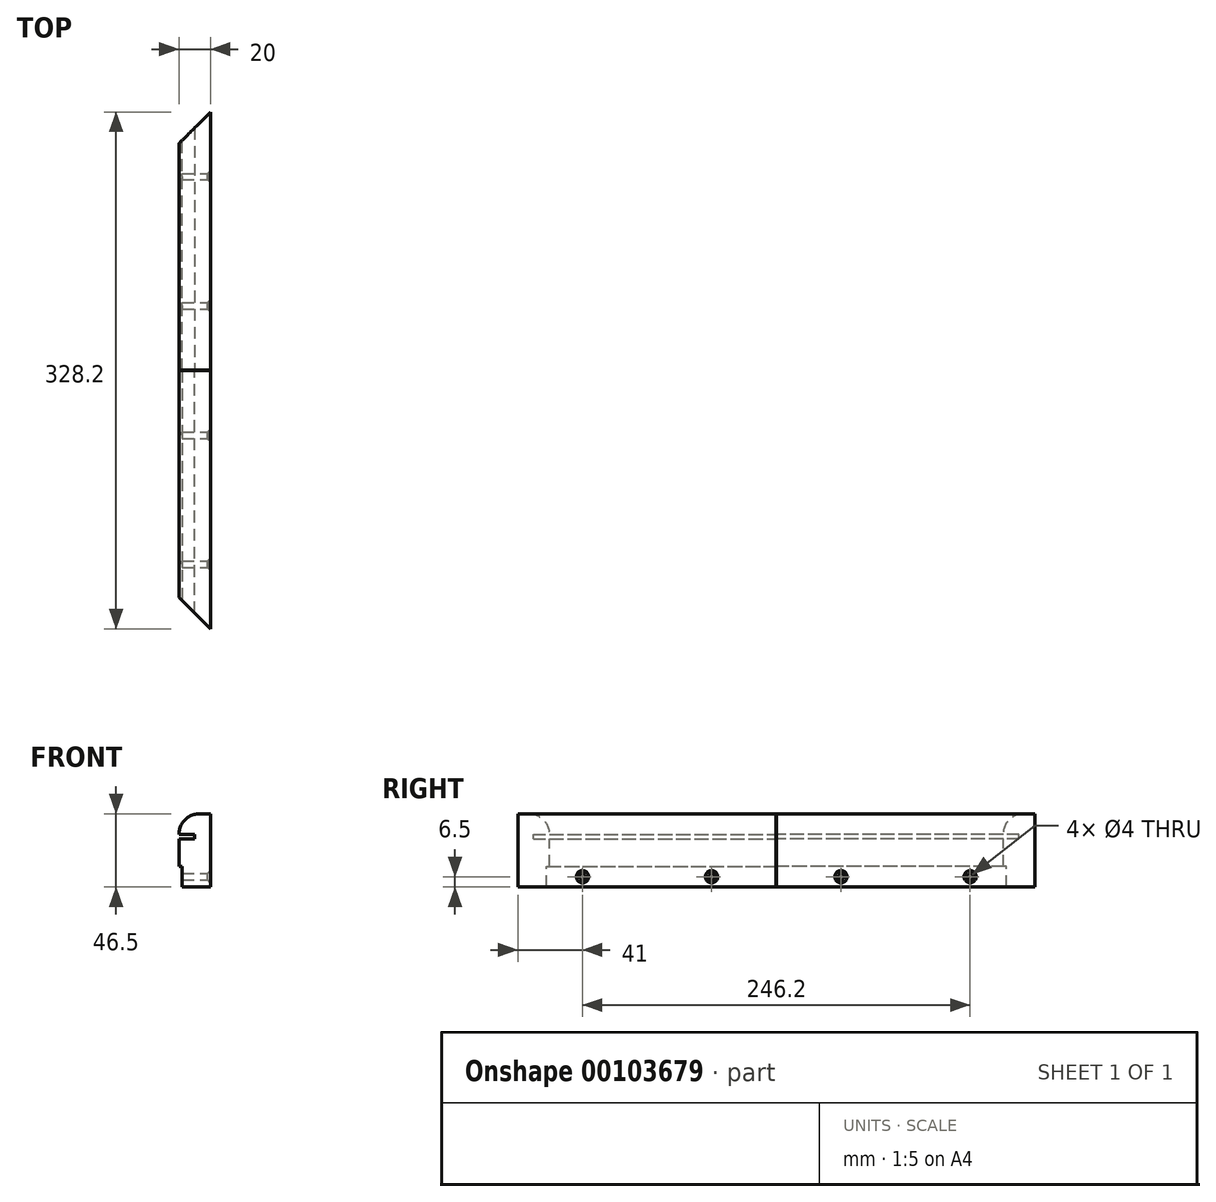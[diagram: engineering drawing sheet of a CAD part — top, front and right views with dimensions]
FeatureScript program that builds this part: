
annotation { "Feature Type Name" : "Feature", "Feature Type Description" : "" }
export const myFeature = defineFeature(function(context is Context, id is Id, definition is map)
    precondition{}
    {
        {
            var Q0;
            Q0=qCreatedBy(makeId("Front.planeOp"),FACE);
            var sketch = newSketch(context, id + "F0", { "sketchPlane" : qUnion([Q0])});
            skLineSegment(sketch, "E0.bottom", {"start": v(10, 23.25) * mm, "end": v(-10, 23.25) * mm});
            skLineSegment(sketch, "E0.top", {"start": v(10, -23.25) * mm, "end": v(-10, -23.25) * mm});
            skLineSegment(sketch, "E0.left", {"start": v(10, 23.25) * mm, "end": v(10, -23.25) * mm});
            skLineSegment(sketch, "E0.right", {"start": v(-10, 23.25) * mm, "end": v(-10, -23.25) * mm});
            skPoint(sketch, "E0.middle", {"position": v(0, 0) * mm});
            skSolve(sketch);
        }
        {
            var Q0;
            Q0=makeQuery(id+"F0.imprint","IMPRINT",FACE,{"disambiguationData":[TD([[makeQuery(id+"F0.imprint","IMPRINT",EDGE,{"derivedFrom":sQuery(id+"F0.wireOp",EDGE,"E0.bottom")}),1.0]])]});
            extrude(context, id + "F1", {"entities" : qUnion([Q0]), "depth" : 164 * mm});
        }
        {
            var Q0;
            Q0=makeQuery(id+"F1.opExtrude","SWEPT_FACE",FACE,{"disambiguationData":[OSD([sQuery(id+"F0.wireOp",EDGE,"E0.right")])]});
            var sketch = newSketch(context, id + "F2", { "sketchPlane" : qUnion([Q0])});
            skLineSegment(sketch, "E1.bottom", {"start": v(0, 10.25) * mm, "end": v(164, 10.25) * mm});
            skLineSegment(sketch, "E1.top", {"start": v(0, 7.15) * mm, "end": v(164, 7.15) * mm});
            skLineSegment(sketch, "E1.left", {"start": v(0, 10.25) * mm, "end": v(0, 7.15) * mm});
            skLineSegment(sketch, "E1.right", {"start": v(164, 10.25) * mm, "end": v(164, 7.15) * mm});
            skLineSegment(sketch, "E2.bottom", {"start": v(0, -23.25) * mm, "end": v(164, -23.25) * mm});
            skLineSegment(sketch, "E2.top", {"start": v(0, -10.25) * mm, "end": v(164, -10.25) * mm});
            skLineSegment(sketch, "E2.left", {"start": v(0, -23.25) * mm, "end": v(0, -10.25) * mm});
            skLineSegment(sketch, "E2.right", {"start": v(164, -23.25) * mm, "end": v(164, -10.25) * mm});
            skSolve(sketch);
        }
        {
            var Q0;
            Q0=makeQuery(id+"F2.imprint","IMPRINT",FACE,{"disambiguationData":[TD([[makeQuery(id+"F2.imprint","IMPRINT",EDGE,{"derivedFrom":sQuery(id+"F2.wireOp",EDGE,"E1.bottom")}),-1.0]])]});
            extrude(context, id + "F3", {"entities" : qUnion([Q0]), "operationType" : NewBodyOperationType.REMOVE, "oppositeDirection" : true, "depth" : 10 * mm});
        }
        {
            var Q0;
            {var subQ0=sQuery(id+"F0.wireOp",EDGE,"E0.right");var subQ2=sQuery(id+"F0.wireOp",EDGE,"E0.top");Q0=makeQuery(id+"F3.boolean.opBoolean","SPLIT",FACE,{"disambiguationData":[TD([makeQuery(id+"F1.opExtrude","SWEPT_FACE",FACE,{"disambiguationData":[OSD([subQ2])]})])],"derivedFrom":makeQuery(id+"F1.opExtrude","SWEPT_FACE",FACE,{"disambiguationData":[OSD([subQ0])]})});}
            var sketch = newSketch(context, id + "F4", { "sketchPlane" : qUnion([Q0])});
            skLineSegment(sketch, "E3.bottom", {"start": v(0, -23.25) * mm, "end": v(164, -23.25) * mm});
            skLineSegment(sketch, "E3.top", {"start": v(0, -10.25) * mm, "end": v(164, -10.25) * mm});
            skLineSegment(sketch, "E3.left", {"start": v(0, -23.25) * mm, "end": v(0, -10.25) * mm});
            skLineSegment(sketch, "E3.right", {"start": v(164, -23.25) * mm, "end": v(164, -10.25) * mm});
            skSolve(sketch);
        }
        {
            var Q0;
            Q0=makeQuery(id+"F4.imprint","IMPRINT",FACE,{"disambiguationData":[TD([[makeQuery(id+"F4.imprint","IMPRINT",EDGE,{"derivedFrom":sQuery(id+"F4.wireOp",EDGE,"E3.bottom")}),-1.0]])]});
            extrude(context, id + "F5", {"entities" : qUnion([Q0]), "operationType" : NewBodyOperationType.REMOVE, "oppositeDirection" : true, "depth" : 2 * mm});
        }
        {
            var Q0;
            Q0=makeQuery(id+"F1.opExtrude","SWEPT_FACE",FACE,{"disambiguationData":[OSD([sQuery(id+"F0.wireOp",EDGE,"E0.bottom")])]});
            var sketch = newSketch(context, id + "F6", { "sketchPlane" : qUnion([Q0])});
            skLineSegment(sketch, "E4.bottom", {"start": v(10, 0) * mm, "end": v(-10, 0) * mm, "construction": true});
            skLineSegment(sketch, "E4.top", {"start": v(10, -20) * mm, "end": v(-10, -20) * mm, "construction": true});
            skLineSegment(sketch, "E4.left", {"start": v(10, 0) * mm, "end": v(10, -20) * mm, "construction": true});
            skLineSegment(sketch, "E4.right", {"start": v(-10, 0) * mm, "end": v(-10, -20) * mm, "construction": true});
            skLineSegment(sketch, "E5", {"start": v(-10, -20) * mm, "end": v(10, 0) * mm});
            skLineSegment(sketch, "E6", {"start": v(-10, -20) * mm, "end": v(-10, 0) * mm});
            skLineSegment(sketch, "E7", {"start": v(-10, 0) * mm, "end": v(10, 0) * mm});
            skSolve(sketch);
        }
        {
            var Q0;
            Q0=makeQuery(id+"F6.imprint","IMPRINT",FACE,{"disambiguationData":[TD([[makeQuery(id+"F6.imprint","IMPRINT",EDGE,{"derivedFrom":sQuery(id+"F6.wireOp",EDGE,"E5")}),1.0]])]});
            var Q1;
            Q1=makeQuery(id+"F1.opExtrude","SWEPT_FACE",FACE,{"disambiguationData":[OSD([sQuery(id+"F0.wireOp",EDGE,"E0.top")])]});
            extrude(context, id + "F7", {"entities" : qUnion([Q0]), "operationType" : NewBodyOperationType.REMOVE, "endBound" : BoundingType.UP_TO_SURFACE, "oppositeDirection" : true, "endBoundEntityFace" : qUnion([Q1]), "depth" : 25 * mm});
        }
        {
            var Q0;
            Q0=makeQuery(id+"F1.opExtrude","SWEPT_EDGE",EDGE,{"disambiguationData":[OSD([sQuery(id+"F0.wireOp",EDGE,"E0.bottom"),sQuery(id+"F0.wireOp",EDGE,"E0.right")])]});
            fillet(context, id + "F8", {"entities" : qUnion([Q0]), "radius" : 13 * mm, "tangentPropagation" : true, "allowEdgeOverflow" : false});
        }
        {
            var Q0;
            Q0=makeQuery(id+"F1.opExtrude","SWEPT_FACE",FACE,{"disambiguationData":[OSD([sQuery(id+"F0.wireOp",EDGE,"E0.left")])]});
            var sketch = newSketch(context, id + "F9", { "sketchPlane" : qUnion([Q0])});
            skLineSegment(sketch, "E8", {"start": v(-82, 23.25) * mm, "end": v(-82, -23.25) * mm, "construction": true});
            skLineSegment(sketch, "E9", {"start": v(-164, -16.75) * mm, "end": v(-82, -16.75) * mm, "construction": true});
            skLineSegment(sketch, "E10", {"start": v(-82, -16.75) * mm, "end": v(0, -16.75) * mm, "construction": true});
            skPoint(sketch, "E11", {"position": v(-123, -16.75) * mm});
            skPoint(sketch, "E12", {"position": v(-41, -16.75) * mm});
            skSolve(sketch);
        }
        {
            var Q0;
            Q0=sQuery(id+"F9.wireOp",VERTEX,"E11");
            var Q1;
            Q1=sQuery(id+"F9.wireOp",VERTEX,"E12");
            var Q2;
            Q2=makeQuery(id+"F1.opExtrude","SWEPT_BODY",BODY,{"disambiguationData":[OSD([sQuery(id+"F0.wireOp",EDGE,"E0.bottom"),sQuery(id+"F0.wireOp",EDGE,"E0.top"),sQuery(id+"F0.wireOp",EDGE,"E0.left"),sQuery(id+"F0.wireOp",EDGE,"E0.right")])]});
            hole(context, id + "F10", {"style" : HoleStyle.C_SINK, "endStyle" : HoleEndStyle.BLIND, "holeDiameter" : 4 * mm, "cSinkDiameter" : 7.8 * mm, "cSinkAngle" : 90 * degree, "holeDepth" : 20 * mm, "tappedDepth" : 12 * mm, "tapClearance" : 3, "locations" : qUnion([Q0, Q1]), "scope" : qUnion([Q2])});
        }
        {
            var Q0;
            Q0=makeQuery(id+"F1.opExtrude","CAP_FACE",FACE,{"disambiguationData":[OSD([sQuery(id+"F0.wireOp",EDGE,"E0.bottom"),sQuery(id+"F0.wireOp",EDGE,"E0.top"),sQuery(id+"F0.wireOp",EDGE,"E0.left"),sQuery(id+"F0.wireOp",EDGE,"E0.right")])],"isStart":false});
            cPlane(context, id + "F11", {"entities" : qUnion([Q0]), "cplaneType" : CPlaneType.OFFSET, "offset" : 0.1 * mm, "width" : 150 * mm, "height" : 150 * mm});
        }
        {
            var Q0;
            Q0=makeQuery(id+"F1.opExtrude","SWEPT_BODY",BODY,{"disambiguationData":[OSD([sQuery(id+"F0.wireOp",EDGE,"E0.bottom"),sQuery(id+"F0.wireOp",EDGE,"E0.top"),sQuery(id+"F0.wireOp",EDGE,"E0.left"),sQuery(id+"F0.wireOp",EDGE,"E0.right")])]});
            var Q1;
            Q1=qCreatedBy(id+"F11.planeOp",FACE);
            mirror(context, id + "F12", {"operationType" : NewBodyOperationType.ADD, "entities" : qUnion([Q0]), "mirrorPlane" : qUnion([Q1])});
        }
    });
